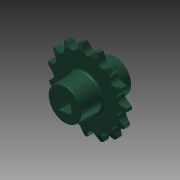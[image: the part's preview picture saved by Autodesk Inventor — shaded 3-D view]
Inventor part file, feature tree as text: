
AUTODESK INVENTOR PART (.ipt)
format: ipt  version: 2013 (Build 170138000, 138)  size: 1,072,128 bytes
history: native  units: mm (DEFAULTED — no unit token found)
features: imported_body x1, sketch x1, other x1, extrude x1
ambient origin geometry x8: Origin, YZ Plane, XZ Plane, XY Plane, X Axis, Y Axis, Z Axis, Center Point
bodies: Solid1 (feature_tree)
feature tree (4):
  imported_body  "Base1"
  sketch  "Sketch1"  dims[d1=2.2606mm d5=25.4mm d6=0.0mm d7=0.0mm d8=0.0mm]
  other  "Srf1"
  extrude  "ExtrusionSrf1"  Depth=25.4mm TaperAngle=0.0deg
